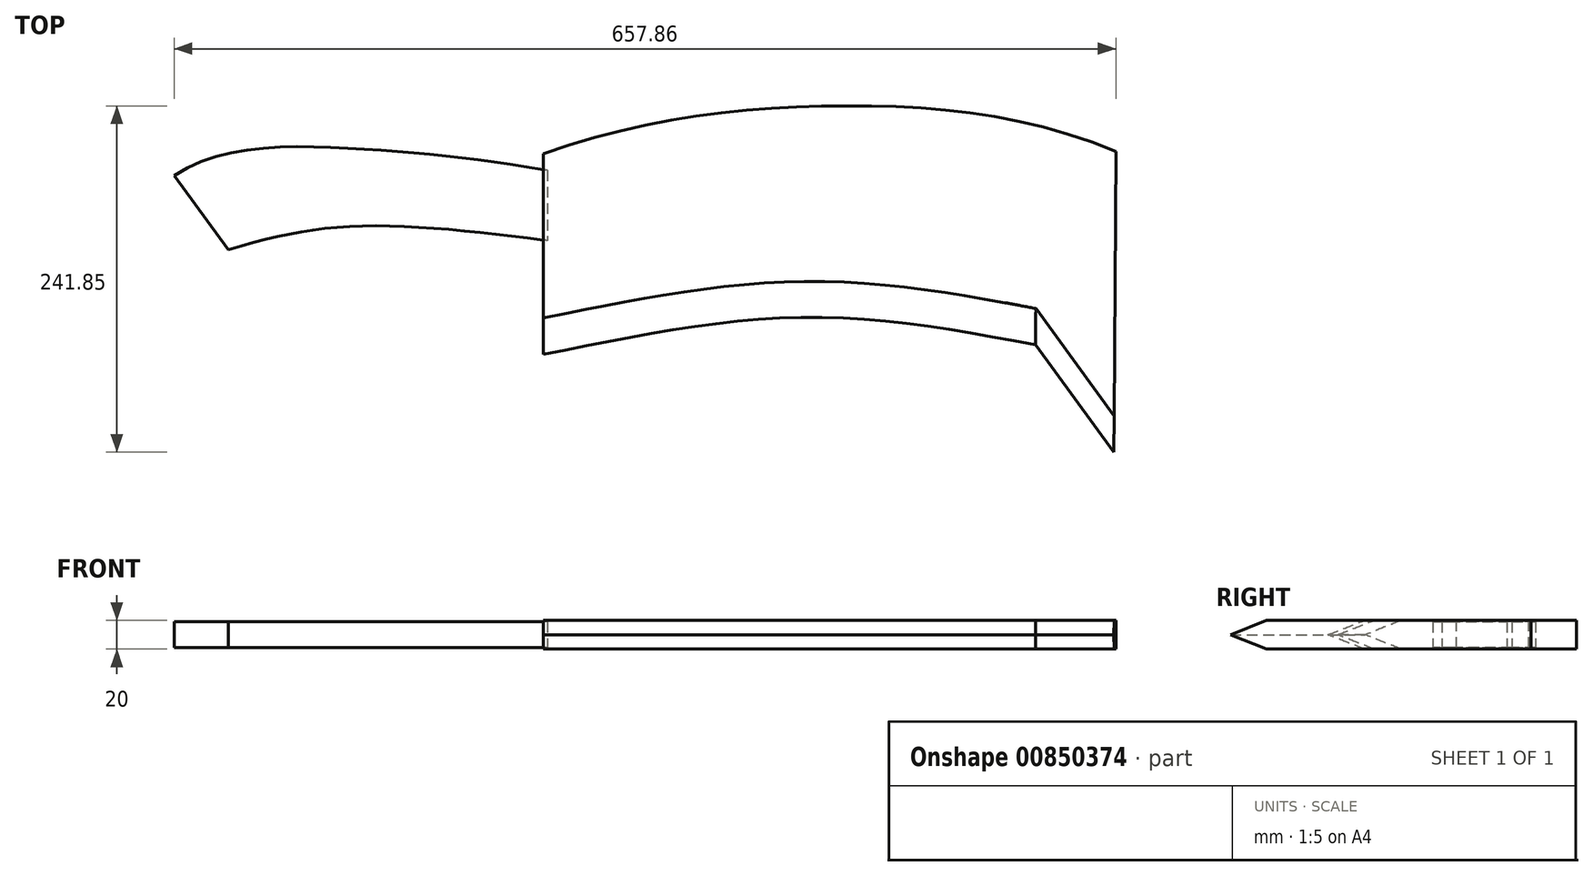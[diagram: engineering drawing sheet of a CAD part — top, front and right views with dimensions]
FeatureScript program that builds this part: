
annotation { "Feature Type Name" : "Feature", "Feature Type Description" : "" }
export const myFeature = defineFeature(function(context is Context, id is Id, definition is map)
    precondition{}
    {
        {
            var Q0;
            Q0=qCreatedBy(makeId("Top.planeOp"),FACE);
            var sketch = newSketch(context, id + "F0", { "sketchPlane" : qUnion([Q0])});
            skFitSpline(sketch, "E0", {"points": [v(-190.82, 30.41) * mm, v(15.49, 63.98) * mm, v(209.18, 32.17) * mm], "startDerivative": vector(414.46, 148.7) * mm, "endDerivative": vector(385.36, -161) * mm});
            skFitSpline(sketch, "E1", {"points": [v(-190.82, -109.59) * mm, v(-7.52, -83.63) * mm, v(153.22, -102.91) * mm], "startDerivative": vector(360.5, 73.54) * mm, "endDerivative": vector(327.83, -61.68) * mm});
            skLineSegment(sketch, "E2", {"start": v(153.22, -102.91) * mm, "end": v(207.7, -177.83) * mm});
            skLineSegment(sketch, "E3", {"start": v(-190.82, 30.41) * mm, "end": v(-190.82, -109.59) * mm});
            skLineSegment(sketch, "E4", {"start": v(209.18, 32.17) * mm, "end": v(207.7, -177.83) * mm});
            skSolve(sketch);
        }
        {
            var Q0;
            Q0=makeQuery(id+"F0.imprint","IMPRINT",FACE,{"disambiguationData":[TD([[makeQuery(id+"F0.imprint","IMPRINT",EDGE,{"derivedFrom":sQuery(id+"F0.wireOp",EDGE,"E0")}),-1.0]])]});
            extrude(context, id + "F1", {"entities" : qUnion([Q0]), "endBound" : BoundingType.SYMMETRIC, "depth" : 20 * mm, "offsetDistance" : 25 * mm});
        }
        {
            var Q0;
            Q0=makeQuery(id+"F1.opExtrude","CAP_EDGE",EDGE,{"disambiguationData":[OSD([sQuery(id+"F0.wireOp",EDGE,"E1")])],"isStart":false});
            var Q1;
            Q1=makeQuery(id+"F1.opExtrude","CAP_EDGE",EDGE,{"disambiguationData":[OSD([sQuery(id+"F0.wireOp",EDGE,"E1")])],"isStart":true});
            chamfer(context, id + "F2", {"entities" : qUnion([Q0, Q1]), "chamferType" : ChamferType.TWO_OFFSETS, "width1" : 25 * mm, "oppositeDirection" : false, "width2" : 10 * mm, "tangentPropagation" : true});
        }
        {
            var Q0;
            Q0=makeQuery(id+"F1.opExtrude","CAP_EDGE",EDGE,{"disambiguationData":[OSD([sQuery(id+"F0.wireOp",EDGE,"E2")])],"isStart":false});
            var Q1;
            Q1=makeQuery(id+"F1.opExtrude","CAP_EDGE",EDGE,{"disambiguationData":[OSD([sQuery(id+"F0.wireOp",EDGE,"E2")])],"isStart":true});
            chamfer(context, id + "F3", {"entities" : qUnion([Q0, Q1]), "chamferType" : ChamferType.TWO_OFFSETS, "width1" : 15 * mm, "oppositeDirection" : false, "width2" : 10 * mm, "tangentPropagation" : true});
        }
        {
            var Q0;
            Q0=qCreatedBy(makeId("Top.planeOp"),FACE);
            var sketch = newSketch(context, id + "F4", { "sketchPlane" : qUnion([Q0])});
            skFitSpline(sketch, "E5", {"points": [v(-190.82, 18.99) * mm, v(-324.6, 34.08) * mm, v(-451.68, 15.2) * mm], "startDerivative": vector(-270.64, 46.88) * mm, "endDerivative": vector(-206.24, -137.5) * mm});
            skFitSpline(sketch, "E6", {"points": [v(-190.82, -30.09) * mm, v(-324.6, -20.02) * mm, v(-413.93, -36.38) * mm], "startDerivative": vector(-257.9, 33.32) * mm, "endDerivative": vector(-211.93, -61.76) * mm});
            skLineSegment(sketch, "E7", {"start": v(-413.93, -36.38) * mm, "end": v(-451.68, 15.2) * mm});
            skLineSegment(sketch, "E8", {"start": v(-190.82, 18.99) * mm, "end": v(-190.82, -30.09) * mm});
            skSolve(sketch);
        }
        {
            var Q0;
            Q0=qSketchRegion(id+"F4",true);
            extrude(context, id + "F5", {"entities" : qUnion([Q0]), "endBound" : BoundingType.SYMMETRIC, "depth" : 18 * mm, "offsetDistance" : 25 * mm});
        }
        {
            var Q0;
            Q0=makeQuery(id+"F5.opExtrude","SWEPT_BODY",BODY,{"disambiguationData":[OSD([sQuery(id+"F4.wireOp",EDGE,"E5"),sQuery(id+"F4.wireOp",EDGE,"E6"),sQuery(id+"F4.wireOp",EDGE,"E7"),sQuery(id+"F4.wireOp",EDGE,"E8")])]});
            transform(context, id + "F6", {"entities" : qUnion([Q0]), "transformType" : TransformType.TRANSLATION_3D, "dx" : 3 * mm, "dy" : 0 * mm, "dz" : 0 * mm, "makeCopy" : false});
        }
    });
